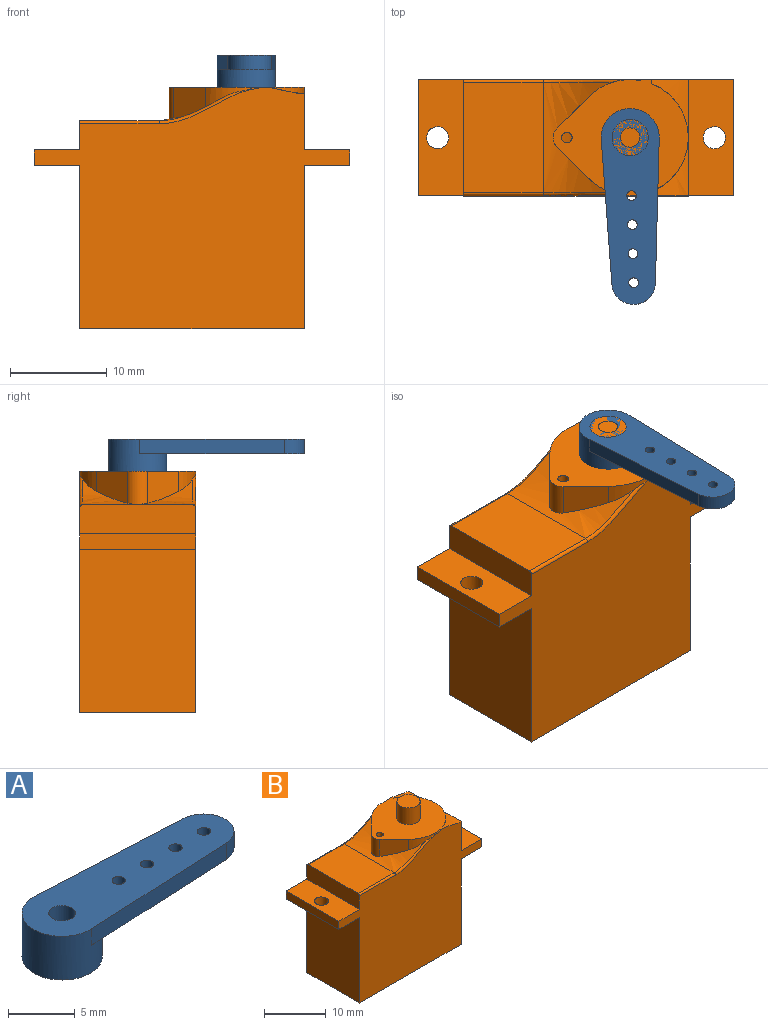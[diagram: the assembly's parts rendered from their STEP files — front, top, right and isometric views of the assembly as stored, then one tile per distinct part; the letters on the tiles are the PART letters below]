
ASSEMBLY  parts=2 mates=1
PART A: 14 faces, bbox 20.3x6x4 mm
  f0: cylinder r=1.7mm len=3.4mm, axis (0,0,1), area 21.4mm2, adj f11,f13
  f1: plane 14.96x1.5mm, normal (0.05,-1,0), area 22.5mm2, adj f2,f8,f9,f10
  f2: cylinder r=2.25mm len=4.49mm, axis (0,0,1), area 10.3mm2, adj f1,f6,f8,f9
  f3: cylinder r=0.5mm len=1.5mm, axis (0,0,1), area 4.7mm2, adj f8,f9
  f4: cylinder r=0.5mm len=1.5mm, axis (0,0,1), area 4.7mm2, adj f8,f9
  f5: cylinder r=0.5mm len=1.5mm, axis (0,0,1), area 4.7mm2, adj f8,f9
  f6: plane 14.96x1.5mm, normal (0.05,1,0), area 22.5mm2, adj f2,f8,f9,f10
  f7: cylinder r=0.5mm len=1.5mm, axis (0,0,1), area 4.7mm2, adj f8,f9
  f8: plane 17.1x5.99mm, normal (0,0,-1), area 69.5mm2, adj f1,f2,f3,f4,f5,f6,f7,f10
  f9: plane 20.25x6mm, normal (0,0,1), area 94.7mm2, adj f1,f2,f3,f4,f5,f6,f7,f10
  f10: cylinder r=3mm len=6mm, axis (0,0,1), area 61.7mm2, adj f1,f6,f8,f9,f11
  f11: plane 6x6mm, normal (0,0,-1), area 19.2mm2, adj f0,f10
  f12: cylinder r=1mm len=2mm, axis (0,0,1), area 12.6mm2, adj f9,f13
  f13: plane 3.4x3.4mm, normal (0,0,-1), area 5.9mm2, adj f0,f12
PART B: 34 faces, bbox 32.7x12.1x28.4 mm
  f0: cylinder r=1.88mm len=3.75mm, axis (0,0,-1), area 38.9mm2, adj f1,f9
  f1: plane 3.75x3.75mm, normal (0,0,1), area 11mm2, adj f0
  f2: plane 3.42x3.4mm, normal (-0.7,0.71,0), area 13.1mm2, adj f3,f6,f9,f12
  f3: cylinder r=1.41mm len=3.35mm, axis (0,0,1), area 7.5mm2, adj f2,f4,f9,f12
  f4: plane 3.42x3.4mm, normal (-0.7,-0.71,0), area 13.1mm2, adj f3,f7,f9,f12
  f5: cylinder r=6mm len=11.17mm, axis (0,0,1), area 4.9mm2, adj f9,f11,f27
  f6: cylinder r=6mm len=5.12mm, axis (0,0,1), area 5.2mm2, adj f2,f9,f12,f29
  f7: cylinder r=6mm len=5.12mm, axis (0,0,1), area 5.2mm2, adj f4,f9,f12,f31
  f8: cylinder r=0.55mm len=2.89mm, axis (0,0,1), area 10mm2, adj f9,f10
  f9: plane 13.96x12.01mm, normal (0,0,1), area 109.2mm2, adj f0,f2,f3,f4,f5,f6,f7,f8
  f10: extruded ~1.1x1.1mm, area 1mm2, adj f8
  f11: extruded ~6x3.81mm, area 7.5mm2, adj f5,f9,f13,f25
  f12: extruded ~11.4x7.13mm, area 42.5mm2, adj f2,f3,f4,f6,f7,f24,f29,f31
  f13: plane 12x5.81mm, normal (1,0,0), area 69.8mm2, adj f11,f23,f25,f26,f27
  f14: plane 12x3mm, normal (-1,0,0), area 36mm2, adj f15,f24,f25,f26,f28,f30
  f15: plane 12x4.7mm, normal (0,0,1), area 52.2mm2, adj f14,f16,f25,f26,f33
  f16: plane 12x1.6mm, normal (-1,0,0), area 19.2mm2, adj f15,f17,f25,f26
  f17: plane 12x4.7mm, normal (0,0,-1), area 52.2mm2, adj f16,f18,f25,f26,f33
  f18: plane 16.9x12mm, normal (-1,0,0), area 202.8mm2, adj f17,f19,f25,f26
  f19: plane 23.2x12mm, normal (0,0,-1), area 278.4mm2, adj f18,f20,f25,f26
  f20: plane 16.9x12mm, normal (1,0,0), area 202.8mm2, adj f19,f21,f25,f26
  f21: plane 12x4.7mm, normal (0,0,-1), area 52.2mm2, adj f20,f22,f25,f26,f32
  f22: plane 12x1.6mm, normal (1,0,0), area 19.2mm2, adj f21,f23,f25,f26
  f23: plane 12x4.7mm, normal (0,0,1), area 52.2mm2, adj f13,f22,f25,f26,f32
  f24: plane 11.4x8.2mm, normal (0,0,1), area 93.5mm2, adj f12,f14,f28,f30
  f25: plane 32.6x25mm, normal (0,-1,0), area 540.6mm2, adj f9,f11,f13,f14,f15,f16,f17,f18
  f26: plane 32.6x25mm, normal (0,1,0), area 540.6mm2, adj f9,f13,f14,f15,f16,f17,f18,f19
  f27: extruded ~6x3.81mm, area 7.5mm2, adj f5,f9,f13,f26
  f28: cylinder r=0.3mm len=8.2mm, axis (-1,0,0), area 3.9mm2, adj f14,f24,f26,f29
  f29: bspline ~20.46x5.48mm, area 4.3mm2, adj f6,f9,f12,f26,f28
  f30: cylinder r=0.3mm len=8.2mm, axis (1,0,0), area 3.9mm2, adj f14,f24,f25,f31
  f31: bspline ~20.46x5.48mm, area 4.3mm2, adj f7,f9,f12,f25,f30
  f32: cylinder r=1.15mm len=2.3mm, axis (0,0,1), area 11.6mm2, adj f21,f23
  f33: cylinder r=1.15mm len=2.3mm, axis (0,0,1), area 11.6mm2, adj f15,f17
PLACE A rot(axis=(0,0,-1),88.6deg) t=(40.21,0,0)mm
PLACE B at identity fixed
MATE revolute A.f12 <-> B.f5  axis (0,0,1) through (40.21,0,0)mm
